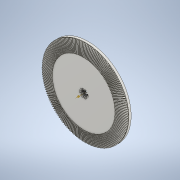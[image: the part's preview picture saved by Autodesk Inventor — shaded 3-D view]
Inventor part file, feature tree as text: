
AUTODESK INVENTOR PART (.ipt)
format: ipt  version: 2021 (Build 250183000, 183)  size: 2,233,856 bytes
history: native  units: mm
features: other x24, loft x2, pattern_circular x2, extrude x2, sketch x2
ambient origin geometry x6: Origin, XZ Plane, X Axis, Y Axis, Z Axis, Center Point
bodies: Solid1 (feature_tree)
feature tree (32):
  other  "Top Point"
  other  "Mesh Plane2"
  other  "Teeth Body"
  other  "Start Point"
  other  "Tooth Plane"
  other  "Start Sketch"
  other  "End Point"
  other  "3D Sketch Right"
  other  "End Plane Right"
  loft  "Loft Right"
  pattern_circular  "Circular Pattern Right"  [2 undecoded]
  other  "3D Sketch Left"
  other  "End Plane Left"
  loft  "Loft Left"
  pattern_circular  "Circular Pattern Left"  Angle=90.0deg  [1 undecoded]
  other  "Fix Body"
  extrude  "Extrusion3"  Depth=5.08mm
  extrude  "Extrusion2"  Depth=5.08mm
  other  "Mesh Plane"
  other  "Top Plane"
  other  "Teeth Body Sketch"
  other  "End Plane"
  other  "End Sketch"
  other  "Helical Curve Left"
  other  "End Sketch Left"
  other  "Body Sketch"
  sketch  "Sketch6"  dims[d0=190.5mm d1=190.082427mm]
  other  "Srf1"
  other  "Helical Curve Right"
  other  "End Sketch Right"
  sketch  "Sketch9"  dims[d2=190.847978mm d3=25.4mm d4=14.831066mm d5=90.0deg d7=198.531719mm d8=188.414636mm d9=514.364825mm d11=25.516417mm d12=146.070909mm d15=138.627204mm d16=378.44702mm d17=0.0mm d18=90.0deg d19=0.0mm d20=90.0deg d21=1800.0mm d22=360.0deg d26=234.767702mm d27=4.194873mm d28=190.5mm d29=-14.056476mm d30=146.070909mm d31=138.627204mm d32=378.44702mm d35=0.0mm d37=0.0mm d39=0.0mm d40=90.0deg d41=1800.0mm d42=360.0deg d46=90.0deg d47=90.0deg d48=0.0mm d49=0.0mm d50=90.0deg d51=0.174533mm d52=0.0mm d53=0.0mm d54=0.0mm d56=11.820524mm d57=581.139965mm d58=577.833731mm d59=427.577232mm d60=425.144651mm d61=427.577232mm d62=425.144651mm d63=90.0deg d64=90.0deg d65=234.767702mm d66=31.5mm d67=190.5mm d68=-14.056476mm d69=4.194873mm d70=138.627204mm d71=378.44702mm d72=146.070909mm d73=425.144651mm d74=427.577232mm d75=0.0mm d76=90.0deg d77=0.0mm d78=90.0deg d79=0.0mm d80=90.0deg d81=1800.0mm d82=360.0deg d84=10.0mm d85=20.0mm d86=20.0mm d87=10.0mm d88=0.0mm d89=0.0mm d90=19.05mm d93=3.175mm d94=3.175mm d95=60.0mm d97=360.0deg d99=0.0mm d100=0.0mm d101=5.08mm d102=0.0mm]
  other  "Pitch Diameter"
note: 3 required parameter values undecoded (feature->parameter linkage not recoverable at this tier; creation-order binding heuristic only, values carry confidence <= 0.55)
